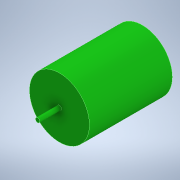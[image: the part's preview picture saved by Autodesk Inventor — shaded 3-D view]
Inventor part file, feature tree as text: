
AUTODESK INVENTOR PART (.ipt)
format: ipt  version: 2022 (Build 260153000, 153)  size: 98,304 bytes
history: native  units: mm
features: extrude x2, sketch x2
ambient origin geometry x8: Origin, YZ Plane, XZ Plane, XY Plane, X Axis, Y Axis, Z Axis, Center Point
bodies: Solid1 (feature_tree)
feature tree (4):
  extrude  "Extrusion1"  Depth=38.0mm TaperAngle=0.0deg
  extrude  "Extrusion2"  Depth=10.0mm TaperAngle=0.0deg
  sketch  "Sketch1"  dims[d0=27.5mm d1=38.0mm d2=0.0mm]
  sketch  "Sketch2"  dims[d3=2.0mm d4=10.0mm d5=0.0mm]
